# Revit family: Down direction governor
name_source: partatom
category: Generic Models
units: mm (PartAtom-declared; Revit-internal decimal feet)

## family parameters
Always vertical = Yes
Can host rebar = No
Cut with Voids When Loaded = No
Part Type = Normal
Room Calculation Point = No
Round Connector Dimension = Use Diameter
Shared = No
Work Plane-Based = No

## types (1)
- Governor Bi-Directional
    Base Plate Height = 8 mm  [stored 0.0262467 ft]
    Base Plate Length = 220 mm  [stored 0.721785 ft]
    Base Plate Mounting Hole Diameter = 16 mm  [stored 0.0524934 ft]
    Base Plate Mounting Hole Positioning = 16 mm  [stored 0.0524934 ft]
    Base Plate Mounting Positioning 2 = 46 mm
    Base Plate Width = 165 mm  [stored 0.541339 ft]
    Default Elevation = 0 mm  [stored 0 ft]
    GovernorType = Bi-directional
    Governor_Diameter = 320 mm  [stored 1.04987 ft]
    Governor_GrooveAngle = 40.00°
    Governor_GrooveDepth = 14 mm  [stored 0.0459318 ft]
    Governor_RatedSpeed = 1.5 m/s
    Groove Width = 12 mm  [stored 0.0393701 ft]
    Inner Groove Width = 5 mm  [stored 0.0164042 ft]
    Mounting Plate Hole Positioning 2 = 78 mm  [stored 0.255906 ft]
    Pulley Centre Line = 170 mm  [stored 0.557743 ft]
    Pulley Groove Depth = 14 mm  [stored 0.0459318 ft]
    Pulley Radius = 158 mm
    Pulley Shaft Diameter = 60 mm  [stored 0.19685 ft]
    Pulley Shaft Radius = 30 mm
    Pulley Support Plate Height = 362 mm  [stored 1.18766 ft]
    Pulley Support Plate Overall Height = 370 mm  [stored 1.21391 ft]
    Pulley Support Plate Thickness = 8 mm  [stored 0.0262467 ft]
    Pulley Support Plate Width = 116 mm  [stored 0.380577 ft]
    Pulley Vertical Centre Line = 16 mm  [stored 0.0524934 ft]
    Pulley Width = 32 mm  [stored 0.104987 ft]

note: [stored X ft] marks values corroborated as IEEE doubles in the binary element streams (Revit-internal decimal feet)

## geometry (parser evidence)
native form markers: Sweep x3
no freeform markers — native parametric forms only
